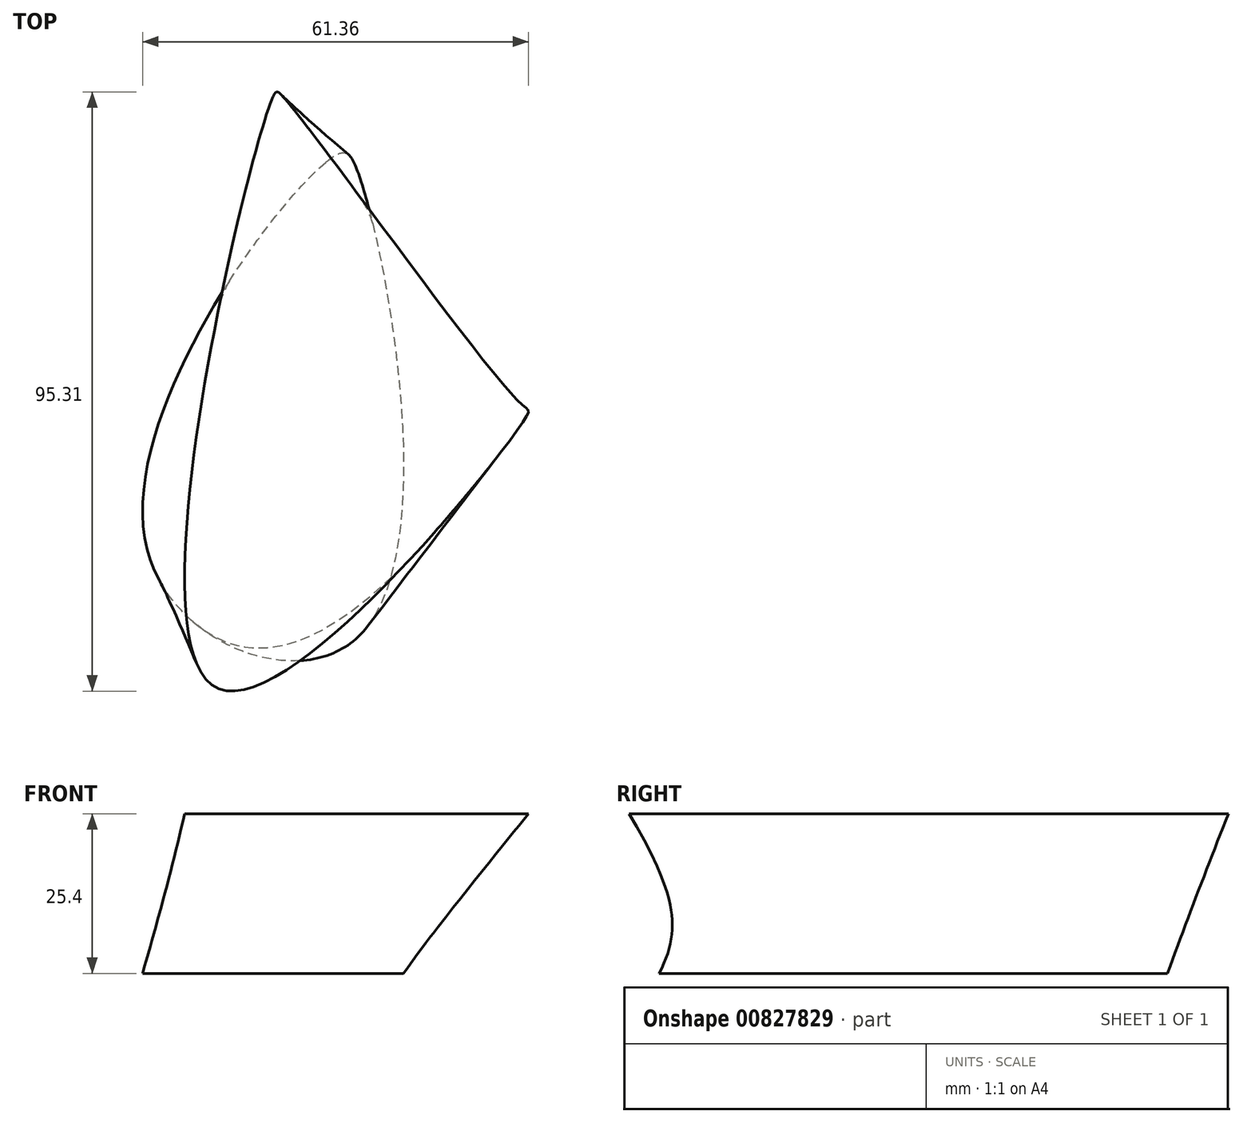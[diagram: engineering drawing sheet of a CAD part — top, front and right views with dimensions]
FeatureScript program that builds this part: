
annotation { "Feature Type Name" : "Feature", "Feature Type Description" : "" }
export const myFeature = defineFeature(function(context is Context, id is Id, definition is map)
    precondition{}
    {
        {
            var Q0;
            Q0=qCreatedBy(makeId("Top.planeOp"),FACE);
            cPlane(context, id + "F0", {"entities" : qUnion([Q0]), "cplaneType" : CPlaneType.OFFSET, "offset" : 25.4 * mm, "width" : 152.4 * mm, "height" : 152.4 * mm});
        }
        {
            var Q0;
            Q0=qCreatedBy(id+"F0.planeOp",FACE);
            var sketch = newSketch(context, id + "F1", { "sketchPlane" : qUnion([Q0])});
            skFitSpline(sketch, "E0", {"points": [v(-140.55, -41.24) * mm, v(-110.87, 20.86) * mm, v(-107.03, 18.65) * mm, v(-106.6, -55.2) * mm, v(-140.55, -41.24) * mm]});
            skSolve(sketch);
        }
        {
            var Q0;
            Q0=qCreatedBy(id+"F0.planeOp",FACE);
            cPlane(context, id + "F2", {"entities" : qUnion([Q0]), "cplaneType" : CPlaneType.OFFSET, "offset" : 25.4 * mm, "width" : 152.4 * mm, "height" : 152.4 * mm});
        }
        {
            var Q0;
            Q0=qCreatedBy(id+"F2.planeOp",FACE);
            var sketch = newSketch(context, id + "F3", { "sketchPlane" : qUnion([Q0])});
            skFitSpline(sketch, "E1", {"points": [v(-120.47, 30.38) * mm, v(-129.56, -63.53) * mm, v(-80.14, -20.43) * mm, v(-81.02, -18.4) * mm, v(-119, 30.59) * mm, v(-120.47, 30.38) * mm]});
            skSolve(sketch);
        }
        {
            var Q0;
            Q0=makeQuery(id+"F3.imprint","IMPRINT",FACE,{"disambiguationData":[TD([[makeQuery(id+"F3.imprint","IMPRINT",EDGE,{"derivedFrom":sQuery(id+"F3.wireOp",EDGE,"E1")}),1.0]])]});
            var Q1;
            Q1=makeQuery(id+"F1.imprint","IMPRINT",FACE,{"disambiguationData":[TD([[makeQuery(id+"F1.imprint","IMPRINT",EDGE,{"derivedFrom":sQuery(id+"F1.wireOp",EDGE,"E0")}),-1.0]])]});
            loft(context, id + "F4", {"sheetProfilesArray" : [{ "sheetProfileEntities" : qUnion([Q0]) }, { "sheetProfileEntities" : qUnion([Q1]) }]});
        }
    });
